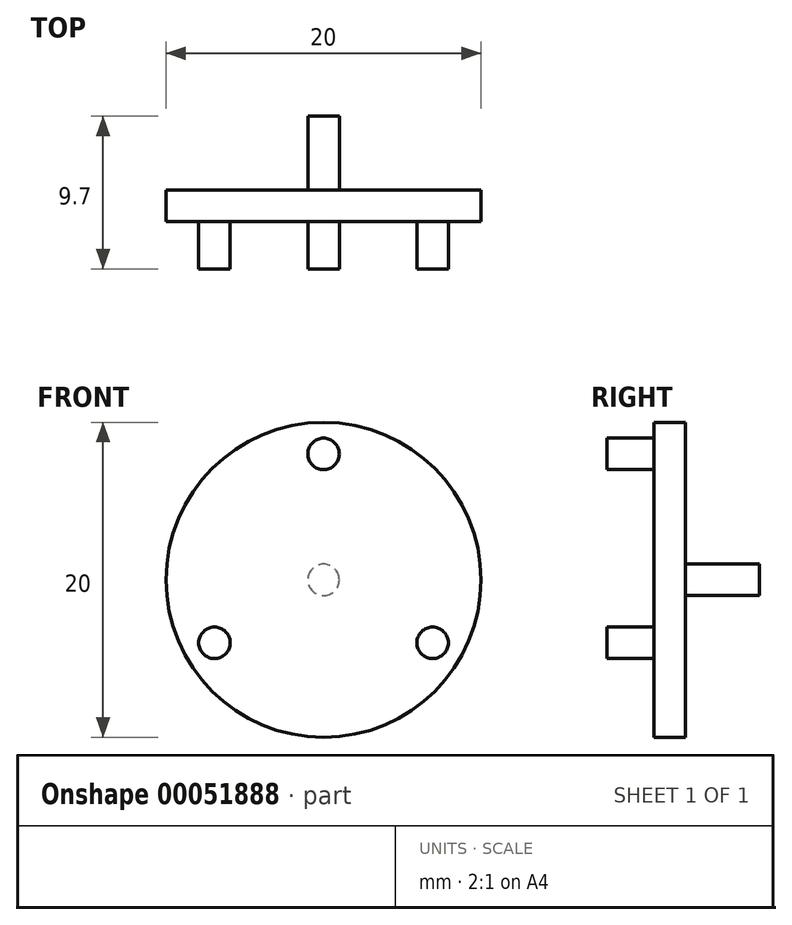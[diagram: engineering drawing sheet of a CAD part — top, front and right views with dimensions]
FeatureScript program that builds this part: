
annotation { "Feature Type Name" : "Feature", "Feature Type Description" : "" }
export const myFeature = defineFeature(function(context is Context, id is Id, definition is map)
    precondition{}
    {
        {
            var Q0;
            Q0=qCreatedBy(makeId("Front.planeOp"),FACE);
            var sketch = newSketch(context, id + "F0", { "sketchPlane" : qUnion([Q0])});
            skCircle(sketch, "E0", {"center": v(0, 0) * mm, "radius": 10 * mm});
            skSolve(sketch);
        }
        {
            var Q0;
            Q0 = qSketchRegion(id + "F0", true);
            extrude(context, id + "F1", {"entities" : qUnion([Q0]), "depth" : 2 * mm});
        }
        {
            var Q0;
            Q0=makeQuery(id+"F1.opExtrude","CAP_FACE",FACE,{"disambiguationData":[OSD([sQuery(id+"F0.wireOp",EDGE,"E0")])],"isStart":false});
            var sketch = newSketch(context, id + "F2", { "sketchPlane" : qUnion([Q0])});
            skCircle(sketch, "E1", {"center": v(0, 0) * mm, "radius": 8 * mm, "construction": true});
            skLineSegment(sketch, "E2", {"start": v(0, 10) * mm, "end": v(0, -10) * mm, "construction": true});
            skLineSegment(sketch, "E3", {"start": v(-10, 0) * mm, "end": v(10, 0) * mm, "construction": true});
            skCircle(sketch, "E4", {"center": v(0, 8) * mm, "radius": 1 * mm});
            skCircle(sketch, "E5.1.0", {"center": v(-6.93, -4) * mm, "radius": 1 * mm});
            skCircle(sketch, "E5.2.0", {"center": v(6.93, -4) * mm, "radius": 1 * mm});
            skSolve(sketch);
        }
        {
            var Q0;
            Q0 = qSketchRegion(id + "F2", true);
            extrude(context, id + "F3", {"entities" : qUnion([Q0]), "operationType" : NewBodyOperationType.ADD, "depth" : 3 * mm});
        }
        {
            var Q0;
            Q0=makeQuery(id+"F1.opExtrude","CAP_FACE",FACE,{"disambiguationData":[OSD([sQuery(id+"F0.wireOp",EDGE,"E0")])],"isStart":true});
            var Q1;
            Q1=makeQuery(id+"F1.opExtrude","CAP_FACE",FACE,{"disambiguationData":[OSD([sQuery(id+"F0.wireOp",EDGE,"E0")])],"isStart":true});
            var sketch = newSketch(context, id + "F4", { "sketchPlane" : qUnion([Q0, Q1])});
            skCircle(sketch, "E6", {"center": v(0, 0) * mm, "radius": 1 * mm});
            skSolve(sketch);
        }
        {
            var Q0;
            Q0 = qSketchRegion(id + "F4", true);
            extrude(context, id + "F5", {"entities" : qUnion([Q0]), "operationType" : NewBodyOperationType.ADD, "depth" : 4.7 * mm});
        }
    });
